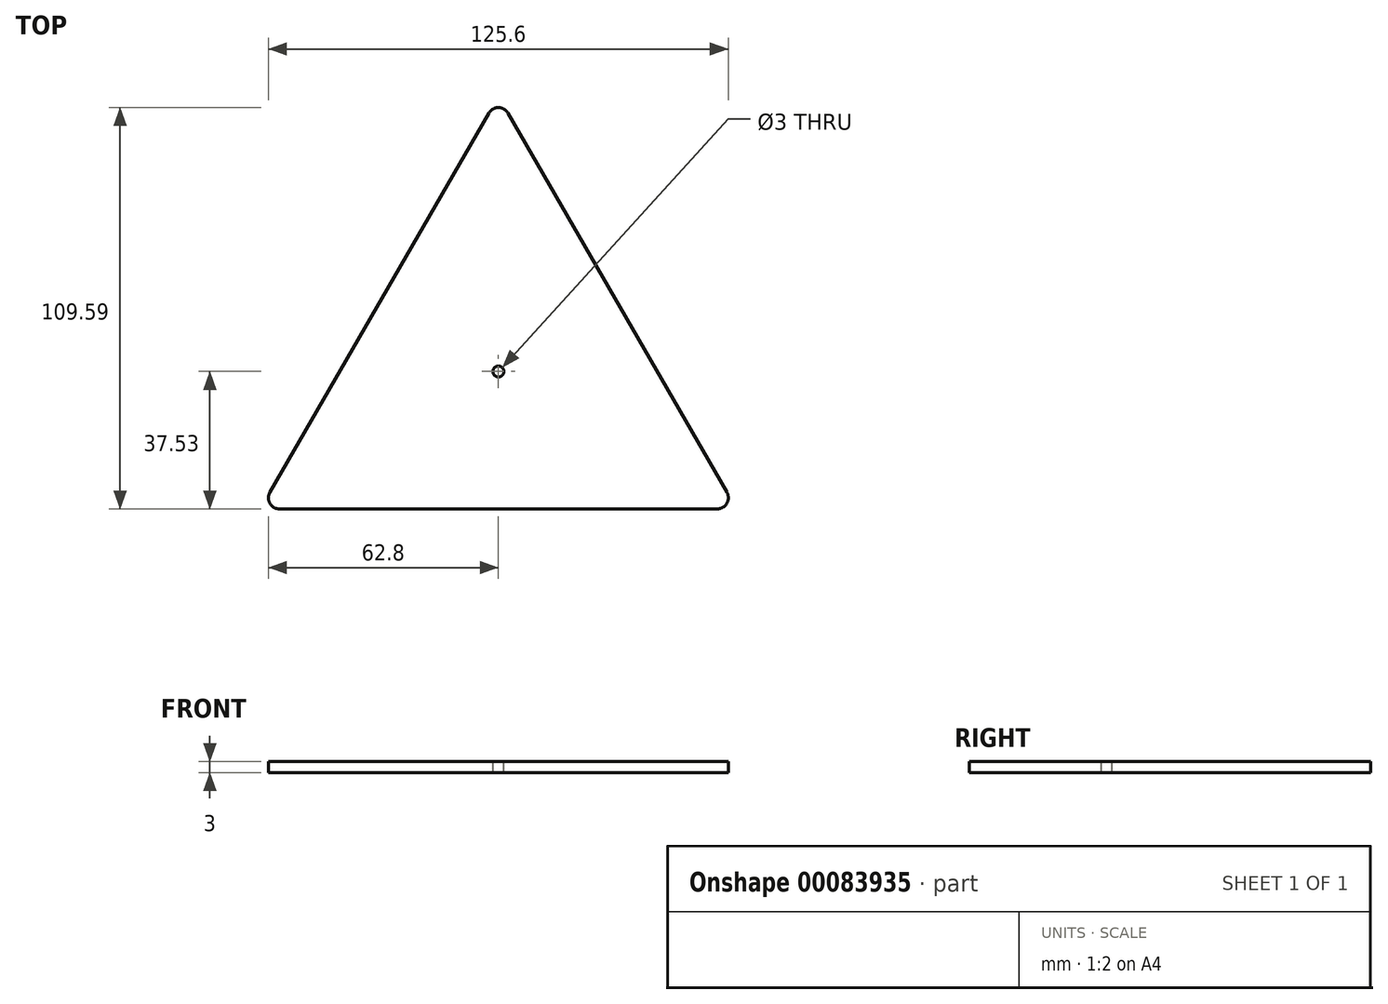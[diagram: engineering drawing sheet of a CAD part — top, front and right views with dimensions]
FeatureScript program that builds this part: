
annotation { "Feature Type Name" : "Feature", "Feature Type Description" : "" }
export const myFeature = defineFeature(function(context is Context, id is Id, definition is map)
    precondition{}
    {
        {
            var Q0;
            Q0=qCreatedBy(makeId("Top.planeOp"),FACE);
            var sketch = newSketch(context, id + "F0", { "sketchPlane" : qUnion([Q0])});
            skCircle(sketch, "E0.cCircle", {"center": v(0, 0) * mm, "radius": 37.53 * mm, "construction": true});
            skLineSegment(sketch, "E0.0", {"start": v(-65, -37.53) * mm, "end": v(0, 75.06) * mm});
            skLineSegment(sketch, "E0.1", {"start": v(0, 75.06) * mm, "end": v(65, -37.53) * mm});
            skLineSegment(sketch, "E0.2", {"start": v(65, -37.53) * mm, "end": v(-65, -37.53) * mm});
            skPoint(sketch, "E0.0.midPoint", {"position": v(-32.5, 18.76) * mm});
            skSolve(sketch);
        }
        {
            var Q0;
            Q0 = qSketchRegion(id + "F0", true);
            extrude(context, id + "F1", {"entities" : qUnion([Q0]), "depth" : 3 * mm});
        }
        {
            var Q0;
            Q0=makeQuery(id+"F1.opExtrude","SWEPT_EDGE",EDGE,{"disambiguationData":[OSD([sQuery(id+"F0.wireOp",EDGE,"E0.0"),sQuery(id+"F0.wireOp",EDGE,"E0.2")])]});
            var Q1;
            Q1=makeQuery(id+"F1.opExtrude","SWEPT_EDGE",EDGE,{"disambiguationData":[OSD([sQuery(id+"F0.wireOp",EDGE,"E0.1"),sQuery(id+"F0.wireOp",EDGE,"E0.2")])]});
            var Q2;
            Q2=makeQuery(id+"F1.opExtrude","SWEPT_EDGE",EDGE,{"disambiguationData":[OSD([sQuery(id+"F0.wireOp",EDGE,"E0.0"),sQuery(id+"F0.wireOp",EDGE,"E0.1")])]});
            fillet(context, id + "F2", {"entities" : qUnion([Q0, Q1, Q2]), "radius" : 3 * mm, "tangentPropagation" : true, "allowEdgeOverflow" : false});
        }
        {
            var Q0;
            Q0=makeQuery(id+"F1.opExtrude","CAP_FACE",FACE,{"disambiguationData":[OSD([sQuery(id+"F0.wireOp",EDGE,"E0.0"),sQuery(id+"F0.wireOp",EDGE,"E0.1"),sQuery(id+"F0.wireOp",EDGE,"E0.2")])],"isStart":false});
            var sketch = newSketch(context, id + "F3", { "sketchPlane" : qUnion([Q0])});
            skCircle(sketch, "E1", {"center": v(0, 0) * mm, "radius": 1.5 * mm});
            skSolve(sketch);
        }
        {
            var Q0;
            Q0 = qSketchRegion(id + "F3", true);
            extrude(context, id + "F4", {"entities" : qUnion([Q0]), "operationType" : NewBodyOperationType.REMOVE, "endBound" : BoundingType.UP_TO_NEXT, "oppositeDirection" : true, "depth" : 25 * mm});
        }
    });
